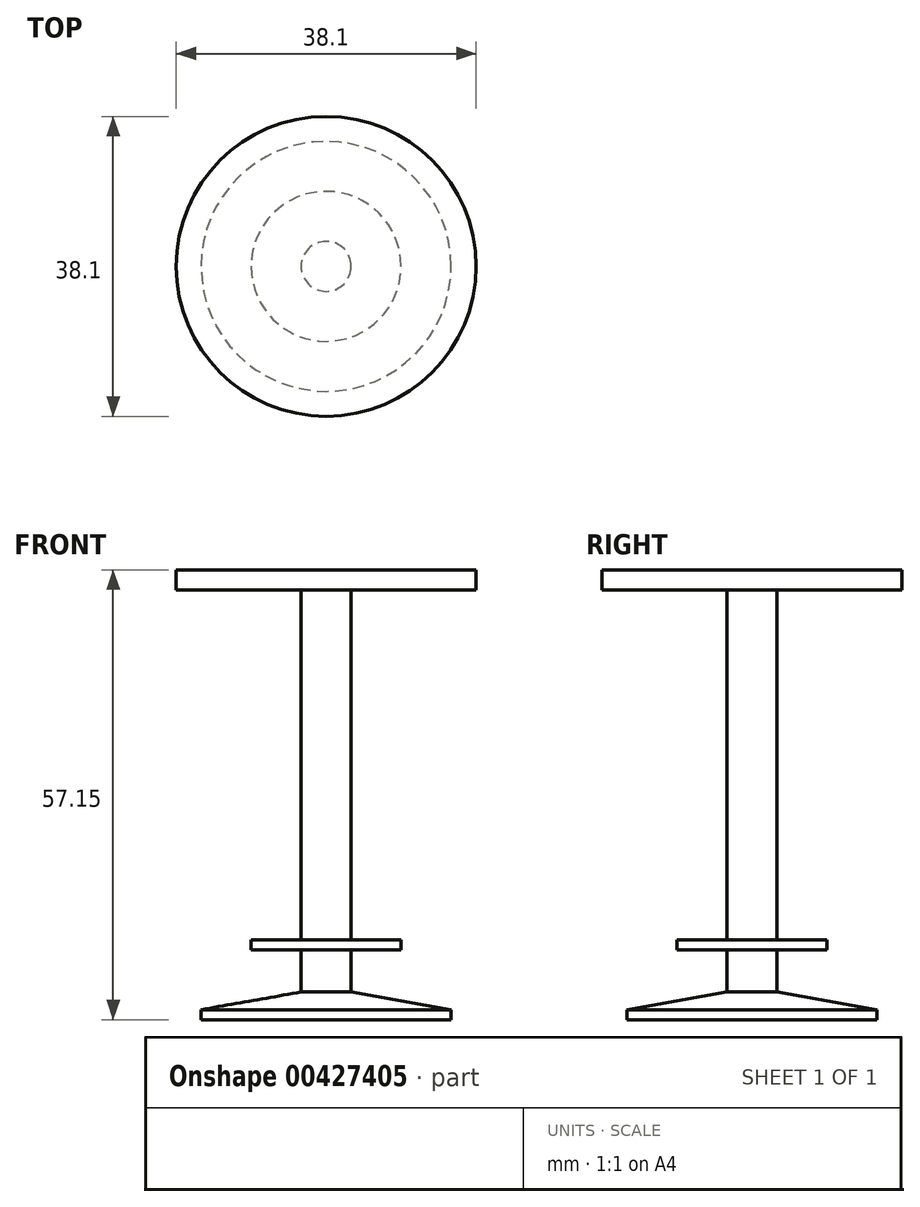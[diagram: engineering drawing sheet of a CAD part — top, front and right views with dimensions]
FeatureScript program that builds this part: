
annotation { "Feature Type Name" : "Feature", "Feature Type Description" : "" }
export const myFeature = defineFeature(function(context is Context, id is Id, definition is map)
    precondition{}
    {
        {
            var Q0;
            Q0=qCreatedBy(makeId("Top.planeOp"),FACE);
            var sketch = newSketch(context, id + "F0", { "sketchPlane" : qUnion([Q0])});
            skCircle(sketch, "E0", {"center": v(0, 0) * mm, "radius": 19.05 * mm});
            skSolve(sketch);
        }
        {
            var Q0;
            Q0 = qSketchRegion(id + "F0", true);
            extrude(context, id + "F1", {"entities" : qUnion([Q0]), "depth" : 2.54 * mm});
        }
        {
            var Q0;
            Q0=makeQuery(id+"F1.opExtrude","CAP_FACE",FACE,{"disambiguationData":[OSD([sQuery(id+"F0.wireOp",EDGE,"E0")])],"isStart":true});
            var sketch = newSketch(context, id + "F2", { "sketchPlane" : qUnion([Q0])});
            skCircle(sketch, "E1", {"center": v(0, 0) * mm, "radius": 3.18 * mm});
            skSolve(sketch);
        }
        {
            var Q0;
            Q0 = qSketchRegion(id + "F2", true);
            extrude(context, id + "F3", {"entities" : qUnion([Q0]), "operationType" : NewBodyOperationType.ADD, "depth" : 44.45 * mm});
        }
        {
            var Q0;
            Q0=makeQuery(id+"F3.opExtrude","CAP_FACE",FACE,{"disambiguationData":[OSD([sQuery(id+"F2.wireOp",EDGE,"E1")])],"isStart":false});
            var sketch = newSketch(context, id + "F4", { "sketchPlane" : qUnion([Q0])});
            skCircle(sketch, "E2", {"center": v(0, 0) * mm, "radius": 9.53 * mm});
            skSolve(sketch);
        }
        {
            var Q0;
            Q0 = qSketchRegion(id + "F4", true);
            extrude(context, id + "F5", {"entities" : qUnion([Q0]), "operationType" : NewBodyOperationType.ADD, "depth" : 1.27 * mm});
        }
        {
            var Q0;
            Q0=makeQuery(id+"F5.opExtrude","CAP_FACE",FACE,{"disambiguationData":[OSD([sQuery(id+"F4.wireOp",EDGE,"E2")])],"isStart":false});
            var sketch = newSketch(context, id + "F6", { "sketchPlane" : qUnion([Q0])});
            skCircle(sketch, "E3", {"center": v(0, 0) * mm, "radius": 3.18 * mm});
            skSolve(sketch);
        }
        {
            var Q0;
            Q0 = qSketchRegion(id + "F6", true);
            extrude(context, id + "F7", {"entities" : qUnion([Q0]), "operationType" : NewBodyOperationType.ADD, "depth" : 5.08 * mm});
        }
        {
            var Q0;
            Q0=makeQuery(id+"F7.opExtrude","CAP_FACE",FACE,{"disambiguationData":[OSD([sQuery(id+"F6.wireOp",EDGE,"E3")])],"isStart":false});
            var sketch = newSketch(context, id + "F8", { "sketchPlane" : qUnion([Q0])});
            skCircle(sketch, "E4", {"center": v(0, 0) * mm, "radius": 15.88 * mm});
            skSolve(sketch);
        }
        {
            var Q0;
            Q0 = qSketchRegion(id + "F8", true);
            extrude(context, id + "F9", {"entities" : qUnion([Q0]), "operationType" : NewBodyOperationType.ADD, "depth" : 3.8 * mm});
        }
        {
            var Q0;
            Q0=makeQuery(id+"F9.opExtrude","CAP_EDGE",EDGE,{"disambiguationData":[OSD([sQuery(id+"F8.wireOp",EDGE,"E4")])],"isStart":true});
            chamfer(context, id + "F10", {"entities" : qUnion([Q0]), "chamferType" : ChamferType.OFFSET_ANGLE, "width" : 2.54 * mm, "oppositeDirection" : false, "angle" : 80 * degree, "tangentPropagation" : true});
        }
    });
